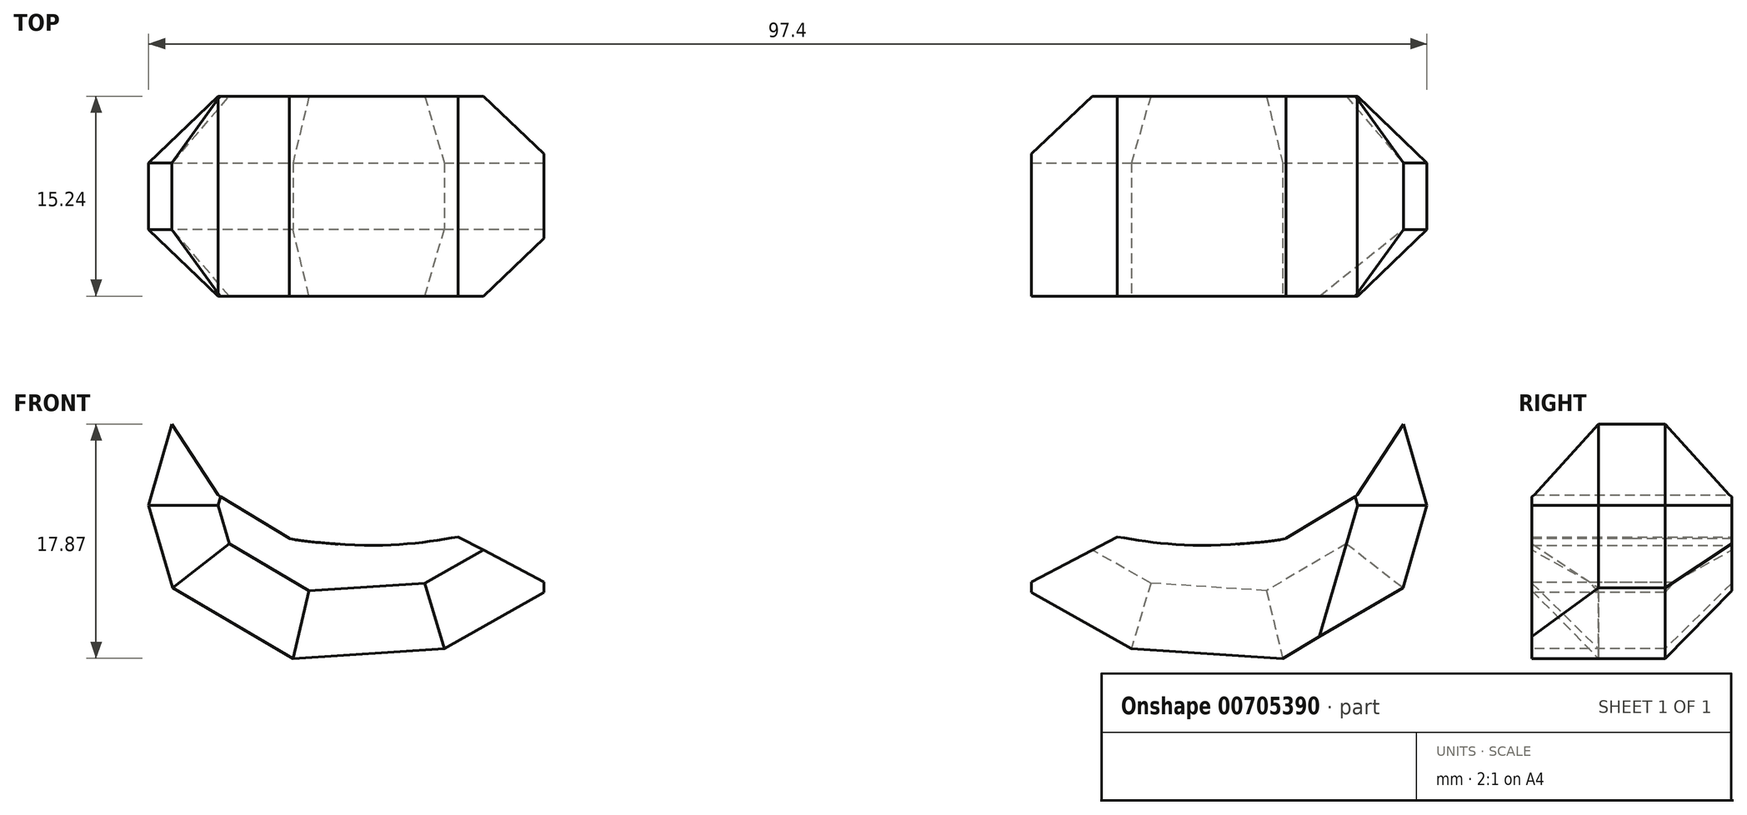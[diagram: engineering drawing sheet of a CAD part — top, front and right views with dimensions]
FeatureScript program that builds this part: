
annotation { "Feature Type Name" : "Feature", "Feature Type Description" : "" }
export const myFeature = defineFeature(function(context is Context, id is Id, definition is map)
    precondition{}
    {
        {
            var Q0;
            Q0=qCreatedBy(makeId("Front.planeOp"),FACE);
            var sketch = newSketch(context, id + "F0", { "sketchPlane" : qUnion([Q0])});
            skLineSegment(sketch, "E0", {"start": v(0, 0) * mm, "end": v(0, -3.04) * mm});
            skLineSegment(sketch, "E1", {"start": v(0, -3.04) * mm, "end": v(0, 0) * mm});
            skLineSegment(sketch, "E2", {"start": v(0, 15.49) * mm, "end": v(-8.28, 1.23) * mm});
            skLineSegment(sketch, "E3", {"start": v(-8.28, 1.23) * mm, "end": v(-12.37, 8.16) * mm});
            skLineSegment(sketch, "E4", {"start": v(-12.37, 8.16) * mm, "end": v(-11.9, 16.15) * mm});
            skFitSpline(sketch, "E5", {"points": [v(-11.9, 16.15) * mm, v(-15.37, 17.85) * mm, v(-17.68, 20.08) * mm, v(-20.4, 22.8) * mm, v(-21.58, 24.61) * mm, v(-23.4, 26.98) * mm], "startDerivative": vector(-17.13, 6.88) * mm, "endDerivative": vector(-10.36, 12.7) * mm});
            skLineSegment(sketch, "E6", {"start": v(-23.4, 26.98) * mm, "end": v(-23.4, 30.61) * mm});
            skLineSegment(sketch, "E7", {"start": v(-23.4, 30.61) * mm, "end": v(-28.49, 20.22) * mm});
            skFitSpline(sketch, "E8", {"points": [v(-28.49, 20.22) * mm, v(-23.37, 15.92) * mm, v(-19.88, 12.37) * mm, v(-18.57, 0.8) * mm], "startDerivative": vector(16.73, -14.68) * mm, "endDerivative": vector(0.35, -32.63) * mm});
            skLineSegment(sketch, "E9", {"start": v(-18.57, 0.8) * mm, "end": v(-25.11, 4.23) * mm});
            skFitSpline(sketch, "E10", {"points": [v(-25.11, 4.23) * mm, v(-32.14, 3.58) * mm, v(-37.97, 4.1) * mm, v(-37.97, 4.11) * mm, v(-37.98, 4.1) * mm], "startDerivative": vector(-12.52, -2.08) * mm, "endDerivative": vector(-0.69, -0.74) * mm});
            skLineSegment(sketch, "E11", {"start": v(-37.97, 4.11) * mm, "end": v(-43.4, 7.41) * mm});
            skLineSegment(sketch, "E12", {"start": v(-43.4, 7.41) * mm, "end": v(-46.92, 12.83) * mm});
            skLineSegment(sketch, "E13", {"start": v(-46.92, 12.83) * mm, "end": v(-48.7, 6.64) * mm});
            skLineSegment(sketch, "E14", {"start": v(-48.7, 6.64) * mm, "end": v(-46.89, 0.36) * mm});
            skLineSegment(sketch, "E15", {"start": v(-46.89, 0.36) * mm, "end": v(-50.1, 2.34) * mm});
            skLineSegment(sketch, "E16", {"start": v(-50.1, 2.34) * mm, "end": v(-54.25, 9.51) * mm});
            skLineSegment(sketch, "E17", {"start": v(-54.25, 9.51) * mm, "end": v(-56.92, 21.51) * mm});
            skLineSegment(sketch, "E18", {"start": v(-56.92, 21.51) * mm, "end": v(-60.41, 10.04) * mm});
            skLineSegment(sketch, "E19", {"start": v(-60.41, 10.04) * mm, "end": v(-59.08, -0.72) * mm});
            skLineSegment(sketch, "E20", {"start": v(-59.08, -0.72) * mm, "end": v(-61.47, 1.15) * mm});
            skLineSegment(sketch, "E21", {"start": v(-61.47, 1.15) * mm, "end": v(-65.53, 8.08) * mm});
            skLineSegment(sketch, "E22", {"start": v(-65.53, 8.08) * mm, "end": v(-66.84, 23.61) * mm});
            skLineSegment(sketch, "E23", {"start": v(-66.84, 23.61) * mm, "end": v(-70.54, 10.04) * mm});
            skLineSegment(sketch, "E24", {"start": v(-70.54, 10.04) * mm, "end": v(-70.54, -4.38) * mm});
            skLineSegment(sketch, "E25", {"start": v(-70.54, -4.38) * mm, "end": v(-64.04, -13.92) * mm});
            skLineSegment(sketch, "E26", {"start": v(-64.04, -13.92) * mm, "end": v(-58.26, -17.24) * mm});
            skLineSegment(sketch, "E27", {"start": v(-58.26, -17.24) * mm, "end": v(-57.47, -21.38) * mm});
            skLineSegment(sketch, "E28", {"start": v(-57.47, -21.38) * mm, "end": v(-50, -19.34) * mm});
            skLineSegment(sketch, "E29", {"start": v(-50, -19.34) * mm, "end": v(-43.4, -18.73) * mm});
            skLineSegment(sketch, "E30", {"start": v(-43.4, -18.73) * mm, "end": v(-31.64, -30.05) * mm});
            skLineSegment(sketch, "E31", {"start": v(-31.64, -30.05) * mm, "end": v(-30.93, -21.53) * mm});
            skLineSegment(sketch, "E32", {"start": v(-30.93, -21.53) * mm, "end": v(-24.8, -15.98) * mm});
            skLineSegment(sketch, "E33", {"start": v(-24.8, -15.98) * mm, "end": v(-12.45, -11.17) * mm});
            skLineSegment(sketch, "E34", {"start": v(-12.45, -11.17) * mm, "end": v(-2.8, -10.37) * mm});
            skLineSegment(sketch, "E35", {"start": v(-2.8, -10.37) * mm, "end": v(0, -15.23) * mm});
            skLineSegment(sketch, "E36", {"start": v(0, -15.23) * mm, "end": v(-2.8, -10.37) * mm});
            skLineSegment(sketch, "E37.MirrorCS", {"start": v(0, 15.49) * mm, "end": v(8.28, 1.23) * mm});
            skLineSegment(sketch, "E38.MirrorCS", {"start": v(0, -15.23) * mm, "end": v(2.8, -10.37) * mm});
            skLineSegment(sketch, "E39.MirrorCS", {"start": v(12.45, -11.17) * mm, "end": v(2.8, -10.37) * mm});
            skLineSegment(sketch, "E40.MirrorCS", {"start": v(8.28, 1.23) * mm, "end": v(12.37, 8.16) * mm});
            skLineSegment(sketch, "E41.MirrorCS", {"start": v(12.37, 8.16) * mm, "end": v(11.9, 16.15) * mm});
            skFitSpline(sketch, "E42.MirrorCS", {"points": [v(11.9, 16.15) * mm, v(15.37, 17.85) * mm, v(17.68, 20.08) * mm, v(20.4, 22.8) * mm, v(21.58, 24.61) * mm, v(23.4, 26.98) * mm], "startDerivative": vector(17.13, 6.88) * mm, "endDerivative": vector(10.36, 12.7) * mm});
            skLineSegment(sketch, "E43.MirrorCS", {"start": v(23.4, 30.61) * mm, "end": v(28.49, 20.22) * mm});
            skLineSegment(sketch, "E44.MirrorCS", {"start": v(23.4, 26.98) * mm, "end": v(23.4, 30.61) * mm});
            skFitSpline(sketch, "E45.MirrorCS", {"points": [v(28.49, 20.22) * mm, v(23.37, 15.92) * mm, v(19.88, 12.37) * mm, v(18.57, 0.8) * mm], "startDerivative": vector(-16.73, -14.68) * mm, "endDerivative": vector(-0.35, -32.63) * mm});
            skLineSegment(sketch, "E46.MirrorCS", {"start": v(18.57, 0.8) * mm, "end": v(25.11, 4.23) * mm});
            skFitSpline(sketch, "E47.MirrorCS", {"points": [v(25.11, 4.23) * mm, v(32.14, 3.58) * mm, v(37.97, 4.1) * mm, v(37.97, 4.11) * mm, v(37.98, 4.1) * mm], "startDerivative": vector(12.52, -2.08) * mm, "endDerivative": vector(0.69, -0.74) * mm});
            skLineSegment(sketch, "E48.MirrorCS", {"start": v(37.97, 4.11) * mm, "end": v(43.4, 7.41) * mm});
            skLineSegment(sketch, "E49.MirrorCS", {"start": v(43.4, 7.41) * mm, "end": v(46.92, 12.83) * mm});
            skLineSegment(sketch, "E50.MirrorCS", {"start": v(46.92, 12.83) * mm, "end": v(48.7, 6.64) * mm});
            skLineSegment(sketch, "E51.MirrorCS", {"start": v(48.7, 6.64) * mm, "end": v(46.89, 0.36) * mm});
            skLineSegment(sketch, "E52.MirrorCS", {"start": v(46.89, 0.36) * mm, "end": v(50.1, 2.34) * mm});
            skLineSegment(sketch, "E53.MirrorCS", {"start": v(50.1, 2.34) * mm, "end": v(54.25, 9.51) * mm});
            skLineSegment(sketch, "E54.MirrorCS", {"start": v(54.25, 9.51) * mm, "end": v(56.92, 21.51) * mm});
            skLineSegment(sketch, "E55.MirrorCS", {"start": v(56.92, 21.51) * mm, "end": v(60.41, 10.04) * mm});
            skLineSegment(sketch, "E56.MirrorCS", {"start": v(60.41, 10.04) * mm, "end": v(59.08, -0.72) * mm});
            skLineSegment(sketch, "E57.MirrorCS", {"start": v(59.08, -0.72) * mm, "end": v(61.47, 1.15) * mm});
            skLineSegment(sketch, "E58.MirrorCS", {"start": v(61.47, 1.15) * mm, "end": v(65.53, 8.08) * mm});
            skLineSegment(sketch, "E59.MirrorCS", {"start": v(65.53, 8.08) * mm, "end": v(66.84, 23.61) * mm});
            skLineSegment(sketch, "E60.MirrorCS", {"start": v(66.84, 23.61) * mm, "end": v(70.54, 10.04) * mm});
            skLineSegment(sketch, "E61.MirrorCS", {"start": v(70.54, 10.04) * mm, "end": v(70.54, -4.38) * mm});
            skLineSegment(sketch, "E62.MirrorCS", {"start": v(70.54, -4.38) * mm, "end": v(64.04, -13.92) * mm});
            skLineSegment(sketch, "E63.MirrorCS", {"start": v(64.04, -13.92) * mm, "end": v(58.26, -17.24) * mm});
            skLineSegment(sketch, "E64.MirrorCS", {"start": v(58.26, -17.24) * mm, "end": v(57.47, -21.38) * mm});
            skLineSegment(sketch, "E65.MirrorCS", {"start": v(57.47, -21.38) * mm, "end": v(50, -19.34) * mm});
            skLineSegment(sketch, "E66.MirrorCS", {"start": v(50, -19.34) * mm, "end": v(43.4, -18.73) * mm});
            skLineSegment(sketch, "E67.MirrorCS", {"start": v(43.4, -18.73) * mm, "end": v(31.64, -30.05) * mm});
            skLineSegment(sketch, "E68.MirrorCS", {"start": v(31.64, -30.05) * mm, "end": v(30.93, -21.53) * mm});
            skLineSegment(sketch, "E69.MirrorCS", {"start": v(30.93, -21.53) * mm, "end": v(24.8, -15.98) * mm});
            skLineSegment(sketch, "E70.MirrorCS", {"start": v(24.8, -15.98) * mm, "end": v(12.45, -11.17) * mm});
            skSolve(sketch);
        }
        {
            var Q0;
            Q0=makeQuery(id+"F0.imprint","IMPRINT",FACE,{"disambiguationData":[TD([[makeQuery(id+"F0.imprint","IMPRINT",EDGE,{"derivedFrom":sQuery(id+"F0.wireOp",EDGE,"E2")}),1.0]])]});
            extrude(context, id + "F1", {"entities" : qUnion([Q0]), "depth" : 7.62 * mm, "offsetDistance" : 25.4 * mm});
        }
        {
            var Q0;
            Q0=makeQuery(id+"F1.opExtrude","CAP_FACE",FACE,{"disambiguationData":[OSD([sQuery(id+"F0.wireOp",EDGE,"E2"),sQuery(id+"F0.wireOp",EDGE,"E3"),sQuery(id+"F0.wireOp",EDGE,"E4"),sQuery(id+"F0.wireOp",EDGE,"E5"),sQuery(id+"F0.wireOp",EDGE,"E6"),sQuery(id+"F0.wireOp",EDGE,"E7"),sQuery(id+"F0.wireOp",EDGE,"E8"),sQuery(id+"F0.wireOp",EDGE,"E9"),sQuery(id+"F0.wireOp",EDGE,"E10"),sQuery(id+"F0.wireOp",EDGE,"E11"),sQuery(id+"F0.wireOp",EDGE,"E12"),sQuery(id+"F0.wireOp",EDGE,"E13"),sQuery(id+"F0.wireOp",EDGE,"E14"),sQuery(id+"F0.wireOp",EDGE,"E15"),sQuery(id+"F0.wireOp",EDGE,"E16"),sQuery(id+"F0.wireOp",EDGE,"E17"),sQuery(id+"F0.wireOp",EDGE,"E18"),sQuery(id+"F0.wireOp",EDGE,"E19"),sQuery(id+"F0.wireOp",EDGE,"E20"),sQuery(id+"F0.wireOp",EDGE,"E21"),sQuery(id+"F0.wireOp",EDGE,"E22"),sQuery(id+"F0.wireOp",EDGE,"E23"),sQuery(id+"F0.wireOp",EDGE,"E24"),sQuery(id+"F0.wireOp",EDGE,"E25"),sQuery(id+"F0.wireOp",EDGE,"E26"),sQuery(id+"F0.wireOp",EDGE,"E27"),sQuery(id+"F0.wireOp",EDGE,"E28"),sQuery(id+"F0.wireOp",EDGE,"E29"),sQuery(id+"F0.wireOp",EDGE,"E30"),sQuery(id+"F0.wireOp",EDGE,"E31"),sQuery(id+"F0.wireOp",EDGE,"E32"),sQuery(id+"F0.wireOp",EDGE,"E33"),sQuery(id+"F0.wireOp",EDGE,"E34"),sQuery(id+"F0.wireOp",EDGE,"E36"),sQuery(id+"F0.wireOp",EDGE,"E37.MirrorCS"),sQuery(id+"F0.wireOp",EDGE,"E38.MirrorCS"),sQuery(id+"F0.wireOp",EDGE,"E39.MirrorCS"),sQuery(id+"F0.wireOp",EDGE,"E40.MirrorCS"),sQuery(id+"F0.wireOp",EDGE,"E41.MirrorCS"),sQuery(id+"F0.wireOp",EDGE,"E42.MirrorCS"),sQuery(id+"F0.wireOp",EDGE,"E43.MirrorCS"),sQuery(id+"F0.wireOp",EDGE,"E44.MirrorCS"),sQuery(id+"F0.wireOp",EDGE,"E45.MirrorCS"),sQuery(id+"F0.wireOp",EDGE,"E46.MirrorCS"),sQuery(id+"F0.wireOp",EDGE,"E47.MirrorCS"),sQuery(id+"F0.wireOp",EDGE,"E48.MirrorCS"),sQuery(id+"F0.wireOp",EDGE,"E49.MirrorCS"),sQuery(id+"F0.wireOp",EDGE,"E50.MirrorCS"),sQuery(id+"F0.wireOp",EDGE,"E51.MirrorCS"),sQuery(id+"F0.wireOp",EDGE,"E52.MirrorCS"),sQuery(id+"F0.wireOp",EDGE,"E53.MirrorCS"),sQuery(id+"F0.wireOp",EDGE,"E54.MirrorCS"),sQuery(id+"F0.wireOp",EDGE,"E55.MirrorCS"),sQuery(id+"F0.wireOp",EDGE,"E56.MirrorCS"),sQuery(id+"F0.wireOp",EDGE,"E57.MirrorCS"),sQuery(id+"F0.wireOp",EDGE,"E58.MirrorCS"),sQuery(id+"F0.wireOp",EDGE,"E59.MirrorCS"),sQuery(id+"F0.wireOp",EDGE,"E60.MirrorCS"),sQuery(id+"F0.wireOp",EDGE,"E61.MirrorCS"),sQuery(id+"F0.wireOp",EDGE,"E62.MirrorCS"),sQuery(id+"F0.wireOp",EDGE,"E63.MirrorCS"),sQuery(id+"F0.wireOp",EDGE,"E64.MirrorCS"),sQuery(id+"F0.wireOp",EDGE,"E65.MirrorCS"),sQuery(id+"F0.wireOp",EDGE,"E66.MirrorCS"),sQuery(id+"F0.wireOp",EDGE,"E67.MirrorCS"),sQuery(id+"F0.wireOp",EDGE,"E68.MirrorCS"),sQuery(id+"F0.wireOp",EDGE,"E69.MirrorCS"),sQuery(id+"F0.wireOp",EDGE,"E70.MirrorCS")])],"isStart":true});
            extrude(context, id + "F2", {"entities" : qUnion([Q0]), "operationType" : NewBodyOperationType.ADD, "depth" : 7.62 * mm, "offsetDistance" : 25.4 * mm});
        }
        {
            var Q0;
            Q0=makeQuery(id+"F1.opExtrude","CAP_FACE",FACE,{"disambiguationData":[OSD([sQuery(id+"F0.wireOp",EDGE,"E2"),sQuery(id+"F0.wireOp",EDGE,"E3"),sQuery(id+"F0.wireOp",EDGE,"E4"),sQuery(id+"F0.wireOp",EDGE,"E5"),sQuery(id+"F0.wireOp",EDGE,"E6"),sQuery(id+"F0.wireOp",EDGE,"E7"),sQuery(id+"F0.wireOp",EDGE,"E8"),sQuery(id+"F0.wireOp",EDGE,"E9"),sQuery(id+"F0.wireOp",EDGE,"E10"),sQuery(id+"F0.wireOp",EDGE,"E11"),sQuery(id+"F0.wireOp",EDGE,"E12"),sQuery(id+"F0.wireOp",EDGE,"E13"),sQuery(id+"F0.wireOp",EDGE,"E14"),sQuery(id+"F0.wireOp",EDGE,"E15"),sQuery(id+"F0.wireOp",EDGE,"E16"),sQuery(id+"F0.wireOp",EDGE,"E17"),sQuery(id+"F0.wireOp",EDGE,"E18"),sQuery(id+"F0.wireOp",EDGE,"E19"),sQuery(id+"F0.wireOp",EDGE,"E20"),sQuery(id+"F0.wireOp",EDGE,"E21"),sQuery(id+"F0.wireOp",EDGE,"E22"),sQuery(id+"F0.wireOp",EDGE,"E23"),sQuery(id+"F0.wireOp",EDGE,"E24"),sQuery(id+"F0.wireOp",EDGE,"E25"),sQuery(id+"F0.wireOp",EDGE,"E26"),sQuery(id+"F0.wireOp",EDGE,"E27"),sQuery(id+"F0.wireOp",EDGE,"E28"),sQuery(id+"F0.wireOp",EDGE,"E29"),sQuery(id+"F0.wireOp",EDGE,"E30"),sQuery(id+"F0.wireOp",EDGE,"E31"),sQuery(id+"F0.wireOp",EDGE,"E32"),sQuery(id+"F0.wireOp",EDGE,"E33"),sQuery(id+"F0.wireOp",EDGE,"E34"),sQuery(id+"F0.wireOp",EDGE,"E36"),sQuery(id+"F0.wireOp",EDGE,"E37.MirrorCS"),sQuery(id+"F0.wireOp",EDGE,"E38.MirrorCS"),sQuery(id+"F0.wireOp",EDGE,"E39.MirrorCS"),sQuery(id+"F0.wireOp",EDGE,"E40.MirrorCS"),sQuery(id+"F0.wireOp",EDGE,"E41.MirrorCS"),sQuery(id+"F0.wireOp",EDGE,"E42.MirrorCS"),sQuery(id+"F0.wireOp",EDGE,"E43.MirrorCS"),sQuery(id+"F0.wireOp",EDGE,"E44.MirrorCS"),sQuery(id+"F0.wireOp",EDGE,"E45.MirrorCS"),sQuery(id+"F0.wireOp",EDGE,"E46.MirrorCS"),sQuery(id+"F0.wireOp",EDGE,"E47.MirrorCS"),sQuery(id+"F0.wireOp",EDGE,"E48.MirrorCS"),sQuery(id+"F0.wireOp",EDGE,"E49.MirrorCS"),sQuery(id+"F0.wireOp",EDGE,"E50.MirrorCS"),sQuery(id+"F0.wireOp",EDGE,"E51.MirrorCS"),sQuery(id+"F0.wireOp",EDGE,"E52.MirrorCS"),sQuery(id+"F0.wireOp",EDGE,"E53.MirrorCS"),sQuery(id+"F0.wireOp",EDGE,"E54.MirrorCS"),sQuery(id+"F0.wireOp",EDGE,"E55.MirrorCS"),sQuery(id+"F0.wireOp",EDGE,"E56.MirrorCS"),sQuery(id+"F0.wireOp",EDGE,"E57.MirrorCS"),sQuery(id+"F0.wireOp",EDGE,"E58.MirrorCS"),sQuery(id+"F0.wireOp",EDGE,"E59.MirrorCS"),sQuery(id+"F0.wireOp",EDGE,"E60.MirrorCS"),sQuery(id+"F0.wireOp",EDGE,"E61.MirrorCS"),sQuery(id+"F0.wireOp",EDGE,"E62.MirrorCS"),sQuery(id+"F0.wireOp",EDGE,"E63.MirrorCS"),sQuery(id+"F0.wireOp",EDGE,"E64.MirrorCS"),sQuery(id+"F0.wireOp",EDGE,"E65.MirrorCS"),sQuery(id+"F0.wireOp",EDGE,"E66.MirrorCS"),sQuery(id+"F0.wireOp",EDGE,"E67.MirrorCS"),sQuery(id+"F0.wireOp",EDGE,"E68.MirrorCS"),sQuery(id+"F0.wireOp",EDGE,"E69.MirrorCS"),sQuery(id+"F0.wireOp",EDGE,"E70.MirrorCS")])],"isStart":false});
            var sketch = newSketch(context, id + "F3", { "sketchPlane" : qUnion([Q0])});
            skLineSegment(sketch, "E71", {"start": v(46.89, 0.36) * mm, "end": v(37.7, -5.04) * mm});
            skLineSegment(sketch, "E72", {"start": v(37.7, -5.04) * mm, "end": v(26.18, -4.3) * mm});
            skLineSegment(sketch, "E73", {"start": v(26.18, -4.3) * mm, "end": v(18.57, 0) * mm});
            skLineSegment(sketch, "E74", {"start": v(18.57, 0) * mm, "end": v(18.57, 0.8) * mm});
            skLineSegment(sketch, "E75", {"start": v(18.57, 0.8) * mm, "end": v(18.57, 0) * mm});
            skLineSegment(sketch, "E76", {"start": v(59.08, -0.72) * mm, "end": v(54.73, -7.1) * mm});
            skLineSegment(sketch, "E77", {"start": v(54.73, -7.1) * mm, "end": v(50.1, -9.58) * mm});
            skLineSegment(sketch, "E78", {"start": v(50.1, -9.58) * mm, "end": v(38.82, -12.7) * mm});
            skLineSegment(sketch, "E79", {"start": v(38.82, -12.7) * mm, "end": v(37.97, -13.2) * mm});
            skLineSegment(sketch, "E80", {"start": v(37.97, -13.2) * mm, "end": v(24.78, -10.64) * mm});
            skLineSegment(sketch, "E81", {"start": v(24.78, -10.64) * mm, "end": v(21.3, -9.07) * mm});
            skLineSegment(sketch, "E82", {"start": v(21.3, -9.07) * mm, "end": v(14.16, -7.03) * mm});
            skLineSegment(sketch, "E83", {"start": v(14.16, -7.03) * mm, "end": v(11.83, 1.15) * mm});
            skLineSegment(sketch, "E84", {"start": v(11.83, 1.15) * mm, "end": v(12.37, 8.16) * mm});
            skLineSegment(sketch, "E85", {"start": v(8.28, 1.23) * mm, "end": v(9, 0) * mm});
            skLineSegment(sketch, "E86", {"start": v(9, 0) * mm, "end": v(2.8, -10.37) * mm});
            skLineSegment(sketch, "E87", {"start": v(2.8, -10.37) * mm, "end": v(9, 0) * mm});
            skLineSegment(sketch, "E88", {"start": v(0, 0) * mm, "end": v(0, -1.55) * mm});
            skLineSegment(sketch, "E89", {"start": v(0, -1.55) * mm, "end": v(0, 0) * mm});
            skLineSegment(sketch, "E90.MirrorCS", {"start": v(-2.8, -10.37) * mm, "end": v(-9, 0) * mm});
            skLineSegment(sketch, "E91.MirrorCS", {"start": v(-8.28, 1.23) * mm, "end": v(-9, 0) * mm});
            skLineSegment(sketch, "E92.MirrorCS", {"start": v(-11.83, 1.15) * mm, "end": v(-12.37, 8.16) * mm});
            skLineSegment(sketch, "E93.MirrorCS", {"start": v(-14.16, -7.03) * mm, "end": v(-11.83, 1.15) * mm});
            skLineSegment(sketch, "E94.MirrorCS", {"start": v(-21.3, -9.07) * mm, "end": v(-14.16, -7.03) * mm});
            skLineSegment(sketch, "E95.MirrorCS", {"start": v(-24.78, -10.64) * mm, "end": v(-21.3, -9.07) * mm});
            skLineSegment(sketch, "E96.MirrorCS", {"start": v(-37.97, -13.2) * mm, "end": v(-24.78, -10.64) * mm});
            skLineSegment(sketch, "E97.MirrorCS", {"start": v(-50.1, -9.58) * mm, "end": v(-38.82, -12.7) * mm});
            skLineSegment(sketch, "E98.MirrorCS", {"start": v(-38.82, -12.7) * mm, "end": v(-37.97, -13.2) * mm});
            skLineSegment(sketch, "E99.MirrorCS", {"start": v(-54.73, -7.1) * mm, "end": v(-50.1, -9.58) * mm});
            skLineSegment(sketch, "E100.MirrorCS", {"start": v(-59.08, -0.72) * mm, "end": v(-54.73, -7.1) * mm});
            skLineSegment(sketch, "E101.MirrorCS", {"start": v(-46.89, 0.36) * mm, "end": v(-37.7, -5.04) * mm});
            skLineSegment(sketch, "E102.MirrorCS", {"start": v(-37.7, -5.04) * mm, "end": v(-26.18, -4.3) * mm});
            skLineSegment(sketch, "E103.MirrorCS", {"start": v(-26.18, -4.3) * mm, "end": v(-18.57, 0) * mm});
            skLineSegment(sketch, "E104.MirrorCS", {"start": v(-18.57, 0.8) * mm, "end": v(-18.57, 0) * mm});
            skSolve(sketch);
        }
        {
            var Q0;
            Q0=makeQuery(id+"F3.imprint","IMPRINT",FACE,{"disambiguationData":[TD([[makeQuery(id+"F3.imprint","IMPRINT",EDGE,{"derivedFrom":sQuery(id+"F3.wireOp",EDGE,"E71")}),1.0]])]});
            var Q1;
            Q1=makeQuery(id+"F3.imprint","IMPRINT",FACE,{"disambiguationData":[TD([[makeQuery(id+"F3.imprint","IMPRINT",EDGE,{"derivedFrom":sQuery(id+"F3.wireOp",EDGE,"E76")}),1.0]])]});
            var Q2;
            Q2=makeQuery(id+"F3.imprint","IMPRINT",FACE,{"disambiguationData":[TD([[makeQuery(id+"F3.imprint","IMPRINT",EDGE,{"derivedFrom":sQuery(id+"F3.wireOp",EDGE,"E85")}),-1.0]])]});
            var Q3;
            Q3=makeQuery(id+"F3.imprint","IMPRINT",FACE,{"disambiguationData":[TD([[makeQuery(id+"F3.imprint","IMPRINT",EDGE,{"derivedFrom":sQuery(id+"F3.wireOp",EDGE,"E90.MirrorCS")}),1.0]])]});
            var Q4;
            Q4=makeQuery(id+"F3.imprint","IMPRINT",FACE,{"disambiguationData":[TD([[makeQuery(id+"F3.imprint","IMPRINT",EDGE,{"derivedFrom":sQuery(id+"F3.wireOp",EDGE,"E92.MirrorCS")}),1.0]])]});
            extrude(context, id + "F4", {"entities" : qUnion([Q0, Q1, Q2, Q3, Q4]), "operationType" : NewBodyOperationType.REMOVE, "oppositeDirection" : true, "depth" : 25.4 * mm, "offsetDistance" : 25.4 * mm});
        }
        {
            var Q0;
            Q0=makeQuery(id+"F4.boolean.opBoolean","COPY",EDGE,{"derivedFrom":makeQuery(id+"F4.opExtrude","CAP_EDGE",EDGE,{"disambiguationData":[OSD([sQuery(id+"F3.wireOp",EDGE,"E72")])],"isStart":true})});
            var Q1;
            Q1=makeQuery(id+"F4.boolean.opBoolean","COPY",EDGE,{"derivedFrom":makeQuery(id+"F4.opExtrude","CAP_EDGE",EDGE,{"disambiguationData":[OSD([sQuery(id+"F3.wireOp",EDGE,"E71")])],"isStart":true})});
            var Q2;
            Q2=makeQuery(id+"F1.opExtrude","CAP_EDGE",EDGE,{"disambiguationData":[OSD([sQuery(id+"F0.wireOp",EDGE,"E51.MirrorCS")])],"isStart":false});
            var Q3;
            Q3=makeQuery(id+"F1.opExtrude","CAP_EDGE",EDGE,{"disambiguationData":[OSD([sQuery(id+"F0.wireOp",EDGE,"E50.MirrorCS")])],"isStart":false});
            var Q4;
            Q4=makeQuery(id+"F4.boolean.opBoolean","COPY",EDGE,{"derivedFrom":makeQuery(id+"F4.opExtrude","CAP_EDGE",EDGE,{"disambiguationData":[OSD([sQuery(id+"F3.wireOp",EDGE,"E103.MirrorCS")])],"isStart":true})});
            var Q5;
            Q5=makeQuery(id+"F4.boolean.opBoolean","COPY",EDGE,{"derivedFrom":makeQuery(id+"F4.opExtrude","CAP_EDGE",EDGE,{"disambiguationData":[OSD([sQuery(id+"F3.wireOp",EDGE,"E102.MirrorCS")])],"isStart":true})});
            var Q6;
            Q6=makeQuery(id+"F4.boolean.opBoolean","COPY",EDGE,{"derivedFrom":makeQuery(id+"F4.opExtrude","CAP_EDGE",EDGE,{"disambiguationData":[OSD([sQuery(id+"F3.wireOp",EDGE,"E101.MirrorCS")])],"isStart":true})});
            var Q7;
            Q7=makeQuery(id+"F1.opExtrude","CAP_EDGE",EDGE,{"disambiguationData":[OSD([sQuery(id+"F0.wireOp",EDGE,"E14")])],"isStart":false});
            var Q8;
            Q8=makeQuery(id+"F1.opExtrude","CAP_EDGE",EDGE,{"disambiguationData":[OSD([sQuery(id+"F0.wireOp",EDGE,"E13")])],"isStart":false});
            chamfer(context, id + "F5", {"entities" : qUnion([Q0, Q1, Q2, Q3, Q4, Q5, Q6, Q7, Q8]), "width" : 5.08 * mm, "tangentPropagation" : true});
        }
        {
            var Q0;
            Q0=makeQuery(id+"F2.opExtrude","CAP_EDGE",EDGE,{"disambiguationData":[OSD([sQuery(id+"F0.wireOp",EDGE,"E13")])],"isStart":false});
            var Q1;
            Q1=makeQuery(id+"F2.opExtrude","CAP_EDGE",EDGE,{"disambiguationData":[OSD([sQuery(id+"F0.wireOp",EDGE,"E14")])],"isStart":false});
            var Q2;
            Q2=makeQuery(id+"F4.boolean.opBoolean","INTERSECT",EDGE,{"derivedFrom":[makeQuery(id+"F2.opExtrude","CAP_FACE",FACE,{"disambiguationData":[OSD([sQuery(id+"F0.wireOp",EDGE,"E2"),sQuery(id+"F0.wireOp",EDGE,"E3"),sQuery(id+"F0.wireOp",EDGE,"E4"),sQuery(id+"F0.wireOp",EDGE,"E5"),sQuery(id+"F0.wireOp",EDGE,"E6"),sQuery(id+"F0.wireOp",EDGE,"E7"),sQuery(id+"F0.wireOp",EDGE,"E8"),sQuery(id+"F0.wireOp",EDGE,"E9"),sQuery(id+"F0.wireOp",EDGE,"E10"),sQuery(id+"F0.wireOp",EDGE,"E11"),sQuery(id+"F0.wireOp",EDGE,"E12"),sQuery(id+"F0.wireOp",EDGE,"E13"),sQuery(id+"F0.wireOp",EDGE,"E14"),sQuery(id+"F0.wireOp",EDGE,"E15"),sQuery(id+"F0.wireOp",EDGE,"E16"),sQuery(id+"F0.wireOp",EDGE,"E17"),sQuery(id+"F0.wireOp",EDGE,"E18"),sQuery(id+"F0.wireOp",EDGE,"E19"),sQuery(id+"F0.wireOp",EDGE,"E20"),sQuery(id+"F0.wireOp",EDGE,"E21"),sQuery(id+"F0.wireOp",EDGE,"E22"),sQuery(id+"F0.wireOp",EDGE,"E23"),sQuery(id+"F0.wireOp",EDGE,"E24"),sQuery(id+"F0.wireOp",EDGE,"E25"),sQuery(id+"F0.wireOp",EDGE,"E26"),sQuery(id+"F0.wireOp",EDGE,"E27"),sQuery(id+"F0.wireOp",EDGE,"E28"),sQuery(id+"F0.wireOp",EDGE,"E29"),sQuery(id+"F0.wireOp",EDGE,"E30"),sQuery(id+"F0.wireOp",EDGE,"E31"),sQuery(id+"F0.wireOp",EDGE,"E32"),sQuery(id+"F0.wireOp",EDGE,"E33"),sQuery(id+"F0.wireOp",EDGE,"E34"),sQuery(id+"F0.wireOp",EDGE,"E36"),sQuery(id+"F0.wireOp",EDGE,"E37.MirrorCS"),sQuery(id+"F0.wireOp",EDGE,"E38.MirrorCS"),sQuery(id+"F0.wireOp",EDGE,"E39.MirrorCS"),sQuery(id+"F0.wireOp",EDGE,"E40.MirrorCS"),sQuery(id+"F0.wireOp",EDGE,"E41.MirrorCS"),sQuery(id+"F0.wireOp",EDGE,"E42.MirrorCS"),sQuery(id+"F0.wireOp",EDGE,"E43.MirrorCS"),sQuery(id+"F0.wireOp",EDGE,"E44.MirrorCS"),sQuery(id+"F0.wireOp",EDGE,"E45.MirrorCS"),sQuery(id+"F0.wireOp",EDGE,"E46.MirrorCS"),sQuery(id+"F0.wireOp",EDGE,"E47.MirrorCS"),sQuery(id+"F0.wireOp",EDGE,"E48.MirrorCS"),sQuery(id+"F0.wireOp",EDGE,"E49.MirrorCS"),sQuery(id+"F0.wireOp",EDGE,"E50.MirrorCS"),sQuery(id+"F0.wireOp",EDGE,"E51.MirrorCS"),sQuery(id+"F0.wireOp",EDGE,"E52.MirrorCS"),sQuery(id+"F0.wireOp",EDGE,"E53.MirrorCS"),sQuery(id+"F0.wireOp",EDGE,"E54.MirrorCS"),sQuery(id+"F0.wireOp",EDGE,"E55.MirrorCS"),sQuery(id+"F0.wireOp",EDGE,"E56.MirrorCS"),sQuery(id+"F0.wireOp",EDGE,"E57.MirrorCS"),sQuery(id+"F0.wireOp",EDGE,"E58.MirrorCS"),sQuery(id+"F0.wireOp",EDGE,"E59.MirrorCS"),sQuery(id+"F0.wireOp",EDGE,"E60.MirrorCS"),sQuery(id+"F0.wireOp",EDGE,"E61.MirrorCS"),sQuery(id+"F0.wireOp",EDGE,"E62.MirrorCS"),sQuery(id+"F0.wireOp",EDGE,"E63.MirrorCS"),sQuery(id+"F0.wireOp",EDGE,"E64.MirrorCS"),sQuery(id+"F0.wireOp",EDGE,"E65.MirrorCS"),sQuery(id+"F0.wireOp",EDGE,"E66.MirrorCS"),sQuery(id+"F0.wireOp",EDGE,"E67.MirrorCS"),sQuery(id+"F0.wireOp",EDGE,"E68.MirrorCS"),sQuery(id+"F0.wireOp",EDGE,"E69.MirrorCS"),sQuery(id+"F0.wireOp",EDGE,"E70.MirrorCS")])],"isStart":false}),makeQuery(id+"F4.opExtrude","SWEPT_FACE",FACE,{"disambiguationData":[OSD([sQuery(id+"F3.wireOp",EDGE,"E101.MirrorCS")])]})]});
            var Q3;
            Q3=makeQuery(id+"F4.boolean.opBoolean","INTERSECT",EDGE,{"derivedFrom":[makeQuery(id+"F2.opExtrude","CAP_FACE",FACE,{"disambiguationData":[OSD([sQuery(id+"F0.wireOp",EDGE,"E2"),sQuery(id+"F0.wireOp",EDGE,"E3"),sQuery(id+"F0.wireOp",EDGE,"E4"),sQuery(id+"F0.wireOp",EDGE,"E5"),sQuery(id+"F0.wireOp",EDGE,"E6"),sQuery(id+"F0.wireOp",EDGE,"E7"),sQuery(id+"F0.wireOp",EDGE,"E8"),sQuery(id+"F0.wireOp",EDGE,"E9"),sQuery(id+"F0.wireOp",EDGE,"E10"),sQuery(id+"F0.wireOp",EDGE,"E11"),sQuery(id+"F0.wireOp",EDGE,"E12"),sQuery(id+"F0.wireOp",EDGE,"E13"),sQuery(id+"F0.wireOp",EDGE,"E14"),sQuery(id+"F0.wireOp",EDGE,"E15"),sQuery(id+"F0.wireOp",EDGE,"E16"),sQuery(id+"F0.wireOp",EDGE,"E17"),sQuery(id+"F0.wireOp",EDGE,"E18"),sQuery(id+"F0.wireOp",EDGE,"E19"),sQuery(id+"F0.wireOp",EDGE,"E20"),sQuery(id+"F0.wireOp",EDGE,"E21"),sQuery(id+"F0.wireOp",EDGE,"E22"),sQuery(id+"F0.wireOp",EDGE,"E23"),sQuery(id+"F0.wireOp",EDGE,"E24"),sQuery(id+"F0.wireOp",EDGE,"E25"),sQuery(id+"F0.wireOp",EDGE,"E26"),sQuery(id+"F0.wireOp",EDGE,"E27"),sQuery(id+"F0.wireOp",EDGE,"E28"),sQuery(id+"F0.wireOp",EDGE,"E29"),sQuery(id+"F0.wireOp",EDGE,"E30"),sQuery(id+"F0.wireOp",EDGE,"E31"),sQuery(id+"F0.wireOp",EDGE,"E32"),sQuery(id+"F0.wireOp",EDGE,"E33"),sQuery(id+"F0.wireOp",EDGE,"E34"),sQuery(id+"F0.wireOp",EDGE,"E36"),sQuery(id+"F0.wireOp",EDGE,"E37.MirrorCS"),sQuery(id+"F0.wireOp",EDGE,"E38.MirrorCS"),sQuery(id+"F0.wireOp",EDGE,"E39.MirrorCS"),sQuery(id+"F0.wireOp",EDGE,"E40.MirrorCS"),sQuery(id+"F0.wireOp",EDGE,"E41.MirrorCS"),sQuery(id+"F0.wireOp",EDGE,"E42.MirrorCS"),sQuery(id+"F0.wireOp",EDGE,"E43.MirrorCS"),sQuery(id+"F0.wireOp",EDGE,"E44.MirrorCS"),sQuery(id+"F0.wireOp",EDGE,"E45.MirrorCS"),sQuery(id+"F0.wireOp",EDGE,"E46.MirrorCS"),sQuery(id+"F0.wireOp",EDGE,"E47.MirrorCS"),sQuery(id+"F0.wireOp",EDGE,"E48.MirrorCS"),sQuery(id+"F0.wireOp",EDGE,"E49.MirrorCS"),sQuery(id+"F0.wireOp",EDGE,"E50.MirrorCS"),sQuery(id+"F0.wireOp",EDGE,"E51.MirrorCS"),sQuery(id+"F0.wireOp",EDGE,"E52.MirrorCS"),sQuery(id+"F0.wireOp",EDGE,"E53.MirrorCS"),sQuery(id+"F0.wireOp",EDGE,"E54.MirrorCS"),sQuery(id+"F0.wireOp",EDGE,"E55.MirrorCS"),sQuery(id+"F0.wireOp",EDGE,"E56.MirrorCS"),sQuery(id+"F0.wireOp",EDGE,"E57.MirrorCS"),sQuery(id+"F0.wireOp",EDGE,"E58.MirrorCS"),sQuery(id+"F0.wireOp",EDGE,"E59.MirrorCS"),sQuery(id+"F0.wireOp",EDGE,"E60.MirrorCS"),sQuery(id+"F0.wireOp",EDGE,"E61.MirrorCS"),sQuery(id+"F0.wireOp",EDGE,"E62.MirrorCS"),sQuery(id+"F0.wireOp",EDGE,"E63.MirrorCS"),sQuery(id+"F0.wireOp",EDGE,"E64.MirrorCS"),sQuery(id+"F0.wireOp",EDGE,"E65.MirrorCS"),sQuery(id+"F0.wireOp",EDGE,"E66.MirrorCS"),sQuery(id+"F0.wireOp",EDGE,"E67.MirrorCS"),sQuery(id+"F0.wireOp",EDGE,"E68.MirrorCS"),sQuery(id+"F0.wireOp",EDGE,"E69.MirrorCS"),sQuery(id+"F0.wireOp",EDGE,"E70.MirrorCS")])],"isStart":false}),makeQuery(id+"F4.opExtrude","SWEPT_FACE",FACE,{"disambiguationData":[OSD([sQuery(id+"F3.wireOp",EDGE,"E102.MirrorCS")])]})]});
            var Q4;
            Q4=makeQuery(id+"F4.boolean.opBoolean","INTERSECT",EDGE,{"derivedFrom":[makeQuery(id+"F2.opExtrude","CAP_FACE",FACE,{"disambiguationData":[OSD([sQuery(id+"F0.wireOp",EDGE,"E2"),sQuery(id+"F0.wireOp",EDGE,"E3"),sQuery(id+"F0.wireOp",EDGE,"E4"),sQuery(id+"F0.wireOp",EDGE,"E5"),sQuery(id+"F0.wireOp",EDGE,"E6"),sQuery(id+"F0.wireOp",EDGE,"E7"),sQuery(id+"F0.wireOp",EDGE,"E8"),sQuery(id+"F0.wireOp",EDGE,"E9"),sQuery(id+"F0.wireOp",EDGE,"E10"),sQuery(id+"F0.wireOp",EDGE,"E11"),sQuery(id+"F0.wireOp",EDGE,"E12"),sQuery(id+"F0.wireOp",EDGE,"E13"),sQuery(id+"F0.wireOp",EDGE,"E14"),sQuery(id+"F0.wireOp",EDGE,"E15"),sQuery(id+"F0.wireOp",EDGE,"E16"),sQuery(id+"F0.wireOp",EDGE,"E17"),sQuery(id+"F0.wireOp",EDGE,"E18"),sQuery(id+"F0.wireOp",EDGE,"E19"),sQuery(id+"F0.wireOp",EDGE,"E20"),sQuery(id+"F0.wireOp",EDGE,"E21"),sQuery(id+"F0.wireOp",EDGE,"E22"),sQuery(id+"F0.wireOp",EDGE,"E23"),sQuery(id+"F0.wireOp",EDGE,"E24"),sQuery(id+"F0.wireOp",EDGE,"E25"),sQuery(id+"F0.wireOp",EDGE,"E26"),sQuery(id+"F0.wireOp",EDGE,"E27"),sQuery(id+"F0.wireOp",EDGE,"E28"),sQuery(id+"F0.wireOp",EDGE,"E29"),sQuery(id+"F0.wireOp",EDGE,"E30"),sQuery(id+"F0.wireOp",EDGE,"E31"),sQuery(id+"F0.wireOp",EDGE,"E32"),sQuery(id+"F0.wireOp",EDGE,"E33"),sQuery(id+"F0.wireOp",EDGE,"E34"),sQuery(id+"F0.wireOp",EDGE,"E36"),sQuery(id+"F0.wireOp",EDGE,"E37.MirrorCS"),sQuery(id+"F0.wireOp",EDGE,"E38.MirrorCS"),sQuery(id+"F0.wireOp",EDGE,"E39.MirrorCS"),sQuery(id+"F0.wireOp",EDGE,"E40.MirrorCS"),sQuery(id+"F0.wireOp",EDGE,"E41.MirrorCS"),sQuery(id+"F0.wireOp",EDGE,"E42.MirrorCS"),sQuery(id+"F0.wireOp",EDGE,"E43.MirrorCS"),sQuery(id+"F0.wireOp",EDGE,"E44.MirrorCS"),sQuery(id+"F0.wireOp",EDGE,"E45.MirrorCS"),sQuery(id+"F0.wireOp",EDGE,"E46.MirrorCS"),sQuery(id+"F0.wireOp",EDGE,"E47.MirrorCS"),sQuery(id+"F0.wireOp",EDGE,"E48.MirrorCS"),sQuery(id+"F0.wireOp",EDGE,"E49.MirrorCS"),sQuery(id+"F0.wireOp",EDGE,"E50.MirrorCS"),sQuery(id+"F0.wireOp",EDGE,"E51.MirrorCS"),sQuery(id+"F0.wireOp",EDGE,"E52.MirrorCS"),sQuery(id+"F0.wireOp",EDGE,"E53.MirrorCS"),sQuery(id+"F0.wireOp",EDGE,"E54.MirrorCS"),sQuery(id+"F0.wireOp",EDGE,"E55.MirrorCS"),sQuery(id+"F0.wireOp",EDGE,"E56.MirrorCS"),sQuery(id+"F0.wireOp",EDGE,"E57.MirrorCS"),sQuery(id+"F0.wireOp",EDGE,"E58.MirrorCS"),sQuery(id+"F0.wireOp",EDGE,"E59.MirrorCS"),sQuery(id+"F0.wireOp",EDGE,"E60.MirrorCS"),sQuery(id+"F0.wireOp",EDGE,"E61.MirrorCS"),sQuery(id+"F0.wireOp",EDGE,"E62.MirrorCS"),sQuery(id+"F0.wireOp",EDGE,"E63.MirrorCS"),sQuery(id+"F0.wireOp",EDGE,"E64.MirrorCS"),sQuery(id+"F0.wireOp",EDGE,"E65.MirrorCS"),sQuery(id+"F0.wireOp",EDGE,"E66.MirrorCS"),sQuery(id+"F0.wireOp",EDGE,"E67.MirrorCS"),sQuery(id+"F0.wireOp",EDGE,"E68.MirrorCS"),sQuery(id+"F0.wireOp",EDGE,"E69.MirrorCS"),sQuery(id+"F0.wireOp",EDGE,"E70.MirrorCS")])],"isStart":false}),makeQuery(id+"F4.opExtrude","SWEPT_FACE",FACE,{"disambiguationData":[OSD([sQuery(id+"F3.wireOp",EDGE,"E103.MirrorCS")])]})]});
            var Q5;
            Q5=makeQuery(id+"F4.boolean.opBoolean","INTERSECT",EDGE,{"derivedFrom":[makeQuery(id+"F2.opExtrude","CAP_FACE",FACE,{"disambiguationData":[OSD([sQuery(id+"F0.wireOp",EDGE,"E2"),sQuery(id+"F0.wireOp",EDGE,"E3"),sQuery(id+"F0.wireOp",EDGE,"E4"),sQuery(id+"F0.wireOp",EDGE,"E5"),sQuery(id+"F0.wireOp",EDGE,"E6"),sQuery(id+"F0.wireOp",EDGE,"E7"),sQuery(id+"F0.wireOp",EDGE,"E8"),sQuery(id+"F0.wireOp",EDGE,"E9"),sQuery(id+"F0.wireOp",EDGE,"E10"),sQuery(id+"F0.wireOp",EDGE,"E11"),sQuery(id+"F0.wireOp",EDGE,"E12"),sQuery(id+"F0.wireOp",EDGE,"E13"),sQuery(id+"F0.wireOp",EDGE,"E14"),sQuery(id+"F0.wireOp",EDGE,"E15"),sQuery(id+"F0.wireOp",EDGE,"E16"),sQuery(id+"F0.wireOp",EDGE,"E17"),sQuery(id+"F0.wireOp",EDGE,"E18"),sQuery(id+"F0.wireOp",EDGE,"E19"),sQuery(id+"F0.wireOp",EDGE,"E20"),sQuery(id+"F0.wireOp",EDGE,"E21"),sQuery(id+"F0.wireOp",EDGE,"E22"),sQuery(id+"F0.wireOp",EDGE,"E23"),sQuery(id+"F0.wireOp",EDGE,"E24"),sQuery(id+"F0.wireOp",EDGE,"E25"),sQuery(id+"F0.wireOp",EDGE,"E26"),sQuery(id+"F0.wireOp",EDGE,"E27"),sQuery(id+"F0.wireOp",EDGE,"E28"),sQuery(id+"F0.wireOp",EDGE,"E29"),sQuery(id+"F0.wireOp",EDGE,"E30"),sQuery(id+"F0.wireOp",EDGE,"E31"),sQuery(id+"F0.wireOp",EDGE,"E32"),sQuery(id+"F0.wireOp",EDGE,"E33"),sQuery(id+"F0.wireOp",EDGE,"E34"),sQuery(id+"F0.wireOp",EDGE,"E36"),sQuery(id+"F0.wireOp",EDGE,"E37.MirrorCS"),sQuery(id+"F0.wireOp",EDGE,"E38.MirrorCS"),sQuery(id+"F0.wireOp",EDGE,"E39.MirrorCS"),sQuery(id+"F0.wireOp",EDGE,"E40.MirrorCS"),sQuery(id+"F0.wireOp",EDGE,"E41.MirrorCS"),sQuery(id+"F0.wireOp",EDGE,"E42.MirrorCS"),sQuery(id+"F0.wireOp",EDGE,"E43.MirrorCS"),sQuery(id+"F0.wireOp",EDGE,"E44.MirrorCS"),sQuery(id+"F0.wireOp",EDGE,"E45.MirrorCS"),sQuery(id+"F0.wireOp",EDGE,"E46.MirrorCS"),sQuery(id+"F0.wireOp",EDGE,"E47.MirrorCS"),sQuery(id+"F0.wireOp",EDGE,"E48.MirrorCS"),sQuery(id+"F0.wireOp",EDGE,"E49.MirrorCS"),sQuery(id+"F0.wireOp",EDGE,"E50.MirrorCS"),sQuery(id+"F0.wireOp",EDGE,"E51.MirrorCS"),sQuery(id+"F0.wireOp",EDGE,"E52.MirrorCS"),sQuery(id+"F0.wireOp",EDGE,"E53.MirrorCS"),sQuery(id+"F0.wireOp",EDGE,"E54.MirrorCS"),sQuery(id+"F0.wireOp",EDGE,"E55.MirrorCS"),sQuery(id+"F0.wireOp",EDGE,"E56.MirrorCS"),sQuery(id+"F0.wireOp",EDGE,"E57.MirrorCS"),sQuery(id+"F0.wireOp",EDGE,"E58.MirrorCS"),sQuery(id+"F0.wireOp",EDGE,"E59.MirrorCS"),sQuery(id+"F0.wireOp",EDGE,"E60.MirrorCS"),sQuery(id+"F0.wireOp",EDGE,"E61.MirrorCS"),sQuery(id+"F0.wireOp",EDGE,"E62.MirrorCS"),sQuery(id+"F0.wireOp",EDGE,"E63.MirrorCS"),sQuery(id+"F0.wireOp",EDGE,"E64.MirrorCS"),sQuery(id+"F0.wireOp",EDGE,"E65.MirrorCS"),sQuery(id+"F0.wireOp",EDGE,"E66.MirrorCS"),sQuery(id+"F0.wireOp",EDGE,"E67.MirrorCS"),sQuery(id+"F0.wireOp",EDGE,"E68.MirrorCS"),sQuery(id+"F0.wireOp",EDGE,"E69.MirrorCS"),sQuery(id+"F0.wireOp",EDGE,"E70.MirrorCS")])],"isStart":false}),makeQuery(id+"F4.opExtrude","SWEPT_FACE",FACE,{"disambiguationData":[OSD([sQuery(id+"F3.wireOp",EDGE,"E73")])]})]});
            var Q6;
            Q6=makeQuery(id+"F4.boolean.opBoolean","INTERSECT",EDGE,{"derivedFrom":[makeQuery(id+"F2.opExtrude","CAP_FACE",FACE,{"disambiguationData":[OSD([sQuery(id+"F0.wireOp",EDGE,"E2"),sQuery(id+"F0.wireOp",EDGE,"E3"),sQuery(id+"F0.wireOp",EDGE,"E4"),sQuery(id+"F0.wireOp",EDGE,"E5"),sQuery(id+"F0.wireOp",EDGE,"E6"),sQuery(id+"F0.wireOp",EDGE,"E7"),sQuery(id+"F0.wireOp",EDGE,"E8"),sQuery(id+"F0.wireOp",EDGE,"E9"),sQuery(id+"F0.wireOp",EDGE,"E10"),sQuery(id+"F0.wireOp",EDGE,"E11"),sQuery(id+"F0.wireOp",EDGE,"E12"),sQuery(id+"F0.wireOp",EDGE,"E13"),sQuery(id+"F0.wireOp",EDGE,"E14"),sQuery(id+"F0.wireOp",EDGE,"E15"),sQuery(id+"F0.wireOp",EDGE,"E16"),sQuery(id+"F0.wireOp",EDGE,"E17"),sQuery(id+"F0.wireOp",EDGE,"E18"),sQuery(id+"F0.wireOp",EDGE,"E19"),sQuery(id+"F0.wireOp",EDGE,"E20"),sQuery(id+"F0.wireOp",EDGE,"E21"),sQuery(id+"F0.wireOp",EDGE,"E22"),sQuery(id+"F0.wireOp",EDGE,"E23"),sQuery(id+"F0.wireOp",EDGE,"E24"),sQuery(id+"F0.wireOp",EDGE,"E25"),sQuery(id+"F0.wireOp",EDGE,"E26"),sQuery(id+"F0.wireOp",EDGE,"E27"),sQuery(id+"F0.wireOp",EDGE,"E28"),sQuery(id+"F0.wireOp",EDGE,"E29"),sQuery(id+"F0.wireOp",EDGE,"E30"),sQuery(id+"F0.wireOp",EDGE,"E31"),sQuery(id+"F0.wireOp",EDGE,"E32"),sQuery(id+"F0.wireOp",EDGE,"E33"),sQuery(id+"F0.wireOp",EDGE,"E34"),sQuery(id+"F0.wireOp",EDGE,"E36"),sQuery(id+"F0.wireOp",EDGE,"E37.MirrorCS"),sQuery(id+"F0.wireOp",EDGE,"E38.MirrorCS"),sQuery(id+"F0.wireOp",EDGE,"E39.MirrorCS"),sQuery(id+"F0.wireOp",EDGE,"E40.MirrorCS"),sQuery(id+"F0.wireOp",EDGE,"E41.MirrorCS"),sQuery(id+"F0.wireOp",EDGE,"E42.MirrorCS"),sQuery(id+"F0.wireOp",EDGE,"E43.MirrorCS"),sQuery(id+"F0.wireOp",EDGE,"E44.MirrorCS"),sQuery(id+"F0.wireOp",EDGE,"E45.MirrorCS"),sQuery(id+"F0.wireOp",EDGE,"E46.MirrorCS"),sQuery(id+"F0.wireOp",EDGE,"E47.MirrorCS"),sQuery(id+"F0.wireOp",EDGE,"E48.MirrorCS"),sQuery(id+"F0.wireOp",EDGE,"E49.MirrorCS"),sQuery(id+"F0.wireOp",EDGE,"E50.MirrorCS"),sQuery(id+"F0.wireOp",EDGE,"E51.MirrorCS"),sQuery(id+"F0.wireOp",EDGE,"E52.MirrorCS"),sQuery(id+"F0.wireOp",EDGE,"E53.MirrorCS"),sQuery(id+"F0.wireOp",EDGE,"E54.MirrorCS"),sQuery(id+"F0.wireOp",EDGE,"E55.MirrorCS"),sQuery(id+"F0.wireOp",EDGE,"E56.MirrorCS"),sQuery(id+"F0.wireOp",EDGE,"E57.MirrorCS"),sQuery(id+"F0.wireOp",EDGE,"E58.MirrorCS"),sQuery(id+"F0.wireOp",EDGE,"E59.MirrorCS"),sQuery(id+"F0.wireOp",EDGE,"E60.MirrorCS"),sQuery(id+"F0.wireOp",EDGE,"E61.MirrorCS"),sQuery(id+"F0.wireOp",EDGE,"E62.MirrorCS"),sQuery(id+"F0.wireOp",EDGE,"E63.MirrorCS"),sQuery(id+"F0.wireOp",EDGE,"E64.MirrorCS"),sQuery(id+"F0.wireOp",EDGE,"E65.MirrorCS"),sQuery(id+"F0.wireOp",EDGE,"E66.MirrorCS"),sQuery(id+"F0.wireOp",EDGE,"E67.MirrorCS"),sQuery(id+"F0.wireOp",EDGE,"E68.MirrorCS"),sQuery(id+"F0.wireOp",EDGE,"E69.MirrorCS"),sQuery(id+"F0.wireOp",EDGE,"E70.MirrorCS")])],"isStart":false}),makeQuery(id+"F4.opExtrude","SWEPT_FACE",FACE,{"disambiguationData":[OSD([sQuery(id+"F3.wireOp",EDGE,"E72")])]})]});
            var Q7;
            Q7=makeQuery(id+"F4.boolean.opBoolean","INTERSECT",EDGE,{"derivedFrom":[makeQuery(id+"F2.opExtrude","CAP_FACE",FACE,{"disambiguationData":[OSD([sQuery(id+"F0.wireOp",EDGE,"E2"),sQuery(id+"F0.wireOp",EDGE,"E3"),sQuery(id+"F0.wireOp",EDGE,"E4"),sQuery(id+"F0.wireOp",EDGE,"E5"),sQuery(id+"F0.wireOp",EDGE,"E6"),sQuery(id+"F0.wireOp",EDGE,"E7"),sQuery(id+"F0.wireOp",EDGE,"E8"),sQuery(id+"F0.wireOp",EDGE,"E9"),sQuery(id+"F0.wireOp",EDGE,"E10"),sQuery(id+"F0.wireOp",EDGE,"E11"),sQuery(id+"F0.wireOp",EDGE,"E12"),sQuery(id+"F0.wireOp",EDGE,"E13"),sQuery(id+"F0.wireOp",EDGE,"E14"),sQuery(id+"F0.wireOp",EDGE,"E15"),sQuery(id+"F0.wireOp",EDGE,"E16"),sQuery(id+"F0.wireOp",EDGE,"E17"),sQuery(id+"F0.wireOp",EDGE,"E18"),sQuery(id+"F0.wireOp",EDGE,"E19"),sQuery(id+"F0.wireOp",EDGE,"E20"),sQuery(id+"F0.wireOp",EDGE,"E21"),sQuery(id+"F0.wireOp",EDGE,"E22"),sQuery(id+"F0.wireOp",EDGE,"E23"),sQuery(id+"F0.wireOp",EDGE,"E24"),sQuery(id+"F0.wireOp",EDGE,"E25"),sQuery(id+"F0.wireOp",EDGE,"E26"),sQuery(id+"F0.wireOp",EDGE,"E27"),sQuery(id+"F0.wireOp",EDGE,"E28"),sQuery(id+"F0.wireOp",EDGE,"E29"),sQuery(id+"F0.wireOp",EDGE,"E30"),sQuery(id+"F0.wireOp",EDGE,"E31"),sQuery(id+"F0.wireOp",EDGE,"E32"),sQuery(id+"F0.wireOp",EDGE,"E33"),sQuery(id+"F0.wireOp",EDGE,"E34"),sQuery(id+"F0.wireOp",EDGE,"E36"),sQuery(id+"F0.wireOp",EDGE,"E37.MirrorCS"),sQuery(id+"F0.wireOp",EDGE,"E38.MirrorCS"),sQuery(id+"F0.wireOp",EDGE,"E39.MirrorCS"),sQuery(id+"F0.wireOp",EDGE,"E40.MirrorCS"),sQuery(id+"F0.wireOp",EDGE,"E41.MirrorCS"),sQuery(id+"F0.wireOp",EDGE,"E42.MirrorCS"),sQuery(id+"F0.wireOp",EDGE,"E43.MirrorCS"),sQuery(id+"F0.wireOp",EDGE,"E44.MirrorCS"),sQuery(id+"F0.wireOp",EDGE,"E45.MirrorCS"),sQuery(id+"F0.wireOp",EDGE,"E46.MirrorCS"),sQuery(id+"F0.wireOp",EDGE,"E47.MirrorCS"),sQuery(id+"F0.wireOp",EDGE,"E48.MirrorCS"),sQuery(id+"F0.wireOp",EDGE,"E49.MirrorCS"),sQuery(id+"F0.wireOp",EDGE,"E50.MirrorCS"),sQuery(id+"F0.wireOp",EDGE,"E51.MirrorCS"),sQuery(id+"F0.wireOp",EDGE,"E52.MirrorCS"),sQuery(id+"F0.wireOp",EDGE,"E53.MirrorCS"),sQuery(id+"F0.wireOp",EDGE,"E54.MirrorCS"),sQuery(id+"F0.wireOp",EDGE,"E55.MirrorCS"),sQuery(id+"F0.wireOp",EDGE,"E56.MirrorCS"),sQuery(id+"F0.wireOp",EDGE,"E57.MirrorCS"),sQuery(id+"F0.wireOp",EDGE,"E58.MirrorCS"),sQuery(id+"F0.wireOp",EDGE,"E59.MirrorCS"),sQuery(id+"F0.wireOp",EDGE,"E60.MirrorCS"),sQuery(id+"F0.wireOp",EDGE,"E61.MirrorCS"),sQuery(id+"F0.wireOp",EDGE,"E62.MirrorCS"),sQuery(id+"F0.wireOp",EDGE,"E63.MirrorCS"),sQuery(id+"F0.wireOp",EDGE,"E64.MirrorCS"),sQuery(id+"F0.wireOp",EDGE,"E65.MirrorCS"),sQuery(id+"F0.wireOp",EDGE,"E66.MirrorCS"),sQuery(id+"F0.wireOp",EDGE,"E67.MirrorCS"),sQuery(id+"F0.wireOp",EDGE,"E68.MirrorCS"),sQuery(id+"F0.wireOp",EDGE,"E69.MirrorCS"),sQuery(id+"F0.wireOp",EDGE,"E70.MirrorCS")])],"isStart":false}),makeQuery(id+"F4.opExtrude","SWEPT_FACE",FACE,{"disambiguationData":[OSD([sQuery(id+"F3.wireOp",EDGE,"E71")])]})]});
            var Q8;
            Q8=makeQuery(id+"F2.opExtrude","CAP_EDGE",EDGE,{"disambiguationData":[OSD([sQuery(id+"F0.wireOp",EDGE,"E51.MirrorCS")])],"isStart":false});
            var Q9;
            Q9=makeQuery(id+"F2.opExtrude","CAP_EDGE",EDGE,{"disambiguationData":[OSD([sQuery(id+"F0.wireOp",EDGE,"E50.MirrorCS")])],"isStart":false});
            chamfer(context, id + "F6", {"entities" : qUnion([Q0, Q1, Q2, Q3, Q4, Q5, Q6, Q7, Q8, Q9]), "width" : 5.08 * mm, "tangentPropagation" : true});
        }
    });
